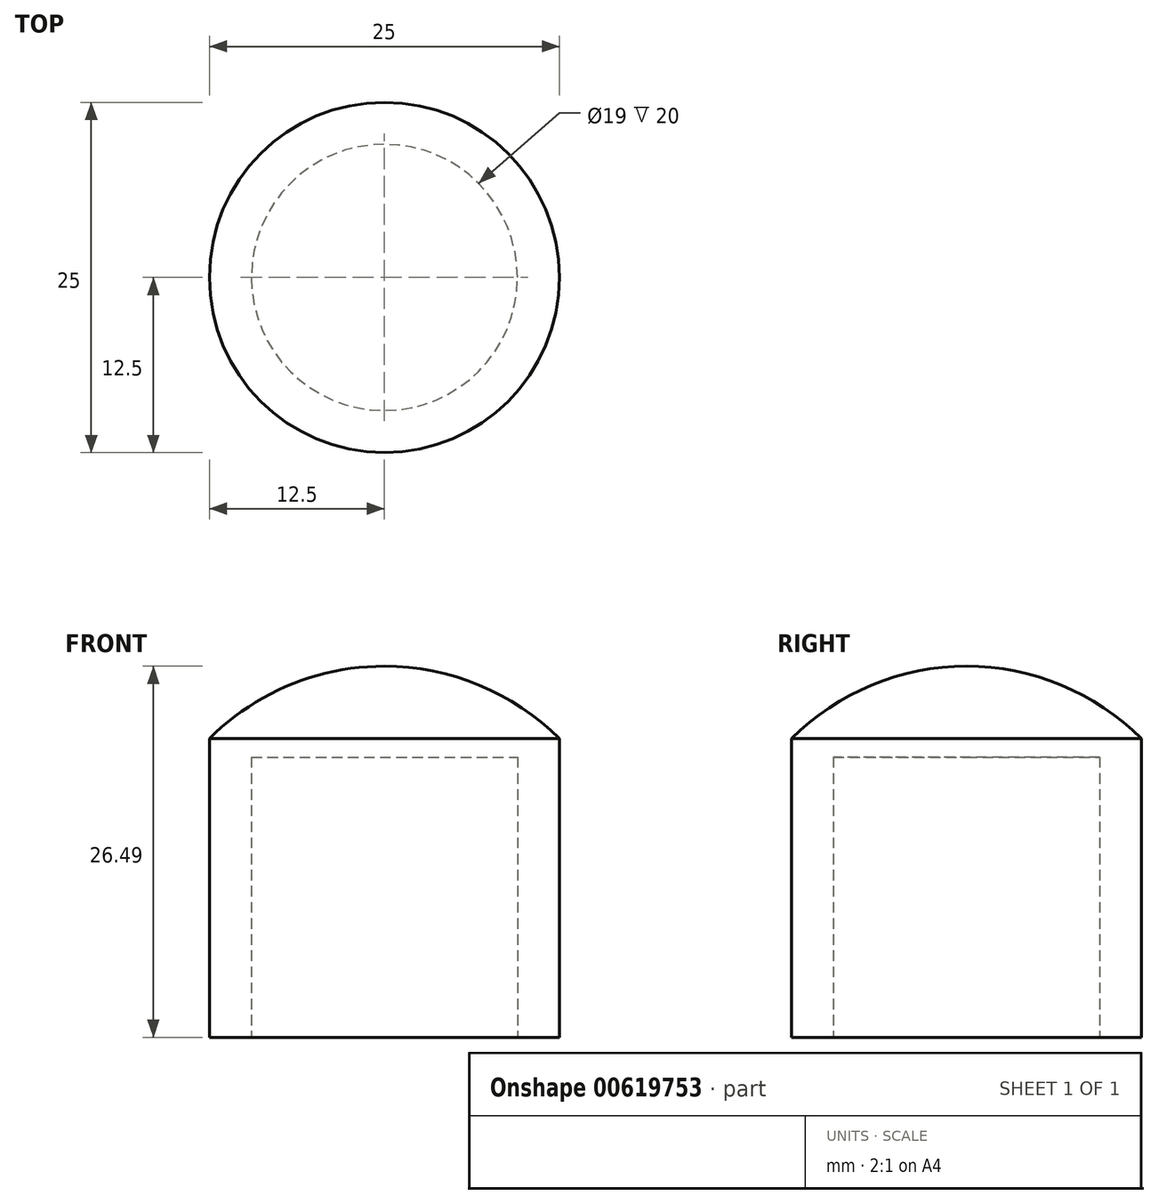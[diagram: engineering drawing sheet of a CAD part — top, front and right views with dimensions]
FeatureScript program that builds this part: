
annotation { "Feature Type Name" : "Feature", "Feature Type Description" : "" }
export const myFeature = defineFeature(function(context is Context, id is Id, definition is map)
    precondition{}
    {
        {
            var Q0;
            Q0=qCreatedBy(makeId("Front.planeOp"),FACE);
            var sketch = newSketch(context, id + "F0", { "sketchPlane" : qUnion([Q0])});
            skLineSegment(sketch, "E0", {"start": v(0, 0) * mm, "end": v(0, 26.49) * mm, "construction": true});
            skLineSegment(sketch, "E1", {"start": v(-9.5, 0) * mm, "end": v(-9.5, 20) * mm});
            skLineSegment(sketch, "E2", {"start": v(-9.5, 20) * mm, "end": v(0, 20) * mm});
            skPoint(sketch, "E2.endSnap0", {"position": v(0, 13.24) * mm});
            skArc(sketch, "E3", {"start": v(-12.5, 21.31) * mm, "mid": v(-6.76, 25.14) * mm, "end": v(0, 26.49) * mm});
            skLineSegment(sketch, "E4", {"start": v(-12.5, 21.31) * mm, "end": v(-12.5, 0) * mm});
            skLineSegment(sketch, "E5", {"start": v(-12.5, 0) * mm, "end": v(-9.5, 0) * mm});
            skLineSegment(sketch, "E6", {"start": v(0, 20) * mm, "end": v(0, 26.49) * mm});
            skCircle(sketch, "E7", {"center": v(-9.5, 20) * mm, "radius": 3 * mm, "construction": true});
            skLineSegment(sketch, "E8", {"start": v(-12.5, 21.31) * mm, "end": v(-17.23, 16.58) * mm, "construction": true});
            skSolve(sketch);
        }
        {
            var Q0;
            Q0 = qSketchRegion(id + "F0", true);
            var Q1;
            Q1=sQuery(id+"F0.wireOp",EDGE,"E0");
            revolve(context, id + "F1", {"entities" : qUnion([Q0]), "axis" : qUnion([Q1]), "revolveType" : RevolveType.FULL});
        }
    });
